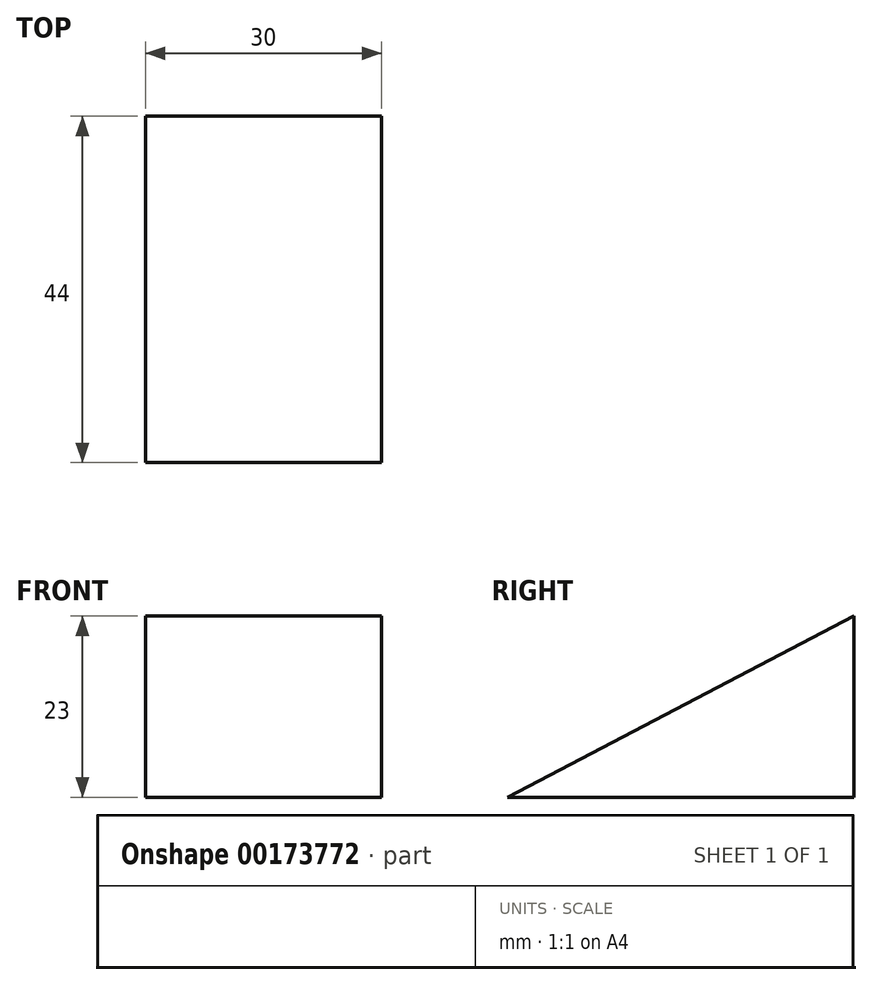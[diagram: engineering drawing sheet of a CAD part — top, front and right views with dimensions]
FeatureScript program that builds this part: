
annotation { "Feature Type Name" : "Feature", "Feature Type Description" : "" }
export const myFeature = defineFeature(function(context is Context, id is Id, definition is map)
    precondition{}
    {
        {
            var Q0;
            Q0=qCreatedBy(makeId("Right.planeOp"),FACE);
            var sketch = newSketch(context, id + "F0", { "sketchPlane" : qUnion([Q0])});
            skLineSegment(sketch, "E0", {"start": v(0, 0) * mm, "end": v(-44, 0) * mm});
            skLineSegment(sketch, "E1", {"start": v(-44, 0) * mm, "end": v(0, 23) * mm});
            skLineSegment(sketch, "E2", {"start": v(0, 23) * mm, "end": v(0, 0) * mm});
            skSolve(sketch);
        }
        {
            var Q0;
            Q0=makeQuery(id+"F0.imprint","IMPRINT",FACE,{"disambiguationData":[TD([[makeQuery(id+"F0.imprint","IMPRINT",EDGE,{"derivedFrom":sQuery(id+"F0.wireOp",EDGE,"E0")}),-1.0]])]});
            extrude(context, id + "F1", {"entities" : qUnion([Q0]), "depth" : 30 * mm});
        }
    });
